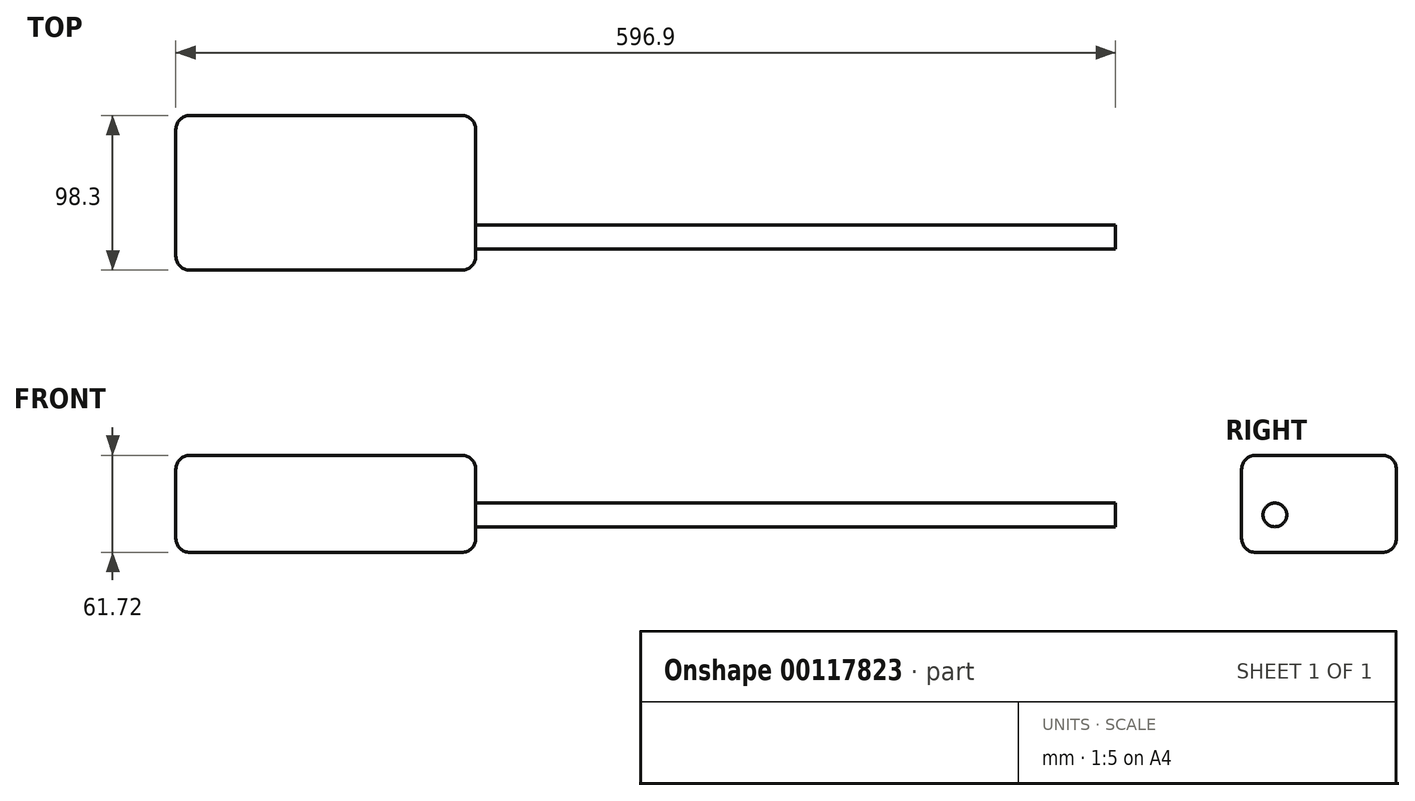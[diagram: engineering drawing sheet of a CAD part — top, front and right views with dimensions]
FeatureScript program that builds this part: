
annotation { "Feature Type Name" : "Feature", "Feature Type Description" : "" }
export const myFeature = defineFeature(function(context is Context, id is Id, definition is map)
    precondition{}
    {
        {
            var Q0;
            Q0=qCreatedBy(makeId("Top.planeOp"),FACE);
            var sketch = newSketch(context, id + "F0", { "sketchPlane" : qUnion([Q0])});
            skLineSegment(sketch, "E0.bottom", {"start": v(-95.25, -49.15) * mm, "end": v(95.25, -49.15) * mm});
            skLineSegment(sketch, "E0.top", {"start": v(-95.25, 49.15) * mm, "end": v(95.25, 49.15) * mm});
            skLineSegment(sketch, "E0.left", {"start": v(-95.25, -49.15) * mm, "end": v(-95.25, 49.15) * mm});
            skLineSegment(sketch, "E0.right", {"start": v(95.25, -49.15) * mm, "end": v(95.25, 49.15) * mm});
            skPoint(sketch, "E0.middle", {"position": v(0, 0) * mm});
            skSolve(sketch);
        }
        {
            var Q0;
            Q0=makeQuery(id+"F0.imprint","IMPRINT",FACE,{"disambiguationData":[TD([[makeQuery(id+"F0.imprint","IMPRINT",EDGE,{"derivedFrom":sQuery(id+"F0.wireOp",EDGE,"E0.bottom")}),1.0]])]});
            extrude(context, id + "F1", {"entities" : qUnion([Q0]), "depth" : 61.72 * mm});
        }
        {
            var Q0;
            Q0=makeQuery(id+"F1.opExtrude","CAP_FACE",FACE,{"disambiguationData":[OSD([sQuery(id+"F0.wireOp",EDGE,"E0.bottom"),sQuery(id+"F0.wireOp",EDGE,"E0.top"),sQuery(id+"F0.wireOp",EDGE,"E0.left"),sQuery(id+"F0.wireOp",EDGE,"E0.right")])],"isStart":true});
            var Q1;
            Q1=makeQuery(id+"F1.opExtrude","SWEPT_FACE",FACE,{"disambiguationData":[OSD([sQuery(id+"F0.wireOp",EDGE,"E0.top")])]});
            var Q2;
            Q2=makeQuery(id+"F1.opExtrude","SWEPT_FACE",FACE,{"disambiguationData":[OSD([sQuery(id+"F0.wireOp",EDGE,"E0.bottom")])]});
            var Q3;
            Q3=makeQuery(id+"F1.opExtrude","CAP_FACE",FACE,{"disambiguationData":[OSD([sQuery(id+"F0.wireOp",EDGE,"E0.bottom"),sQuery(id+"F0.wireOp",EDGE,"E0.top"),sQuery(id+"F0.wireOp",EDGE,"E0.left"),sQuery(id+"F0.wireOp",EDGE,"E0.right")])],"isStart":false});
            fillet(context, id + "F2", {"entities" : qUnion([Q0, Q1, Q2, Q3]), "radius" : 8.9 * mm, "tangentPropagation" : true, "allowEdgeOverflow" : false});
        }
        {
            var Q0;
            Q0=makeQuery(id+"F1.opExtrude","SWEPT_FACE",FACE,{"disambiguationData":[OSD([sQuery(id+"F0.wireOp",EDGE,"E0.right")])]});
            var sketch = newSketch(context, id + "F3", { "sketchPlane" : qUnion([Q0])});
            skCircle(sketch, "E1", {"center": v(-28.04, 23.84) * mm, "radius": 7.54 * mm});
            skSolve(sketch);
        }
        {
            var Q0;
            Q0 = qSketchRegion(id + "F3", true);
            var Q1;
            Q1=makeQuery(id+"F3.imprint","IMPRINT",FACE,{"disambiguationData":[TD([[makeQuery(id+"F3.imprint","IMPRINT",EDGE,{"derivedFrom":sQuery(id+"F3.wireOp",EDGE,"E1")}),1.0]])]});
            extrude(context, id + "F4", {"entities" : qUnion([Q0, Q1]), "operationType" : NewBodyOperationType.ADD, "depth" : 406.4 * mm});
        }
    });
